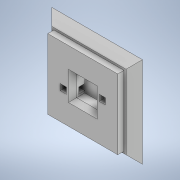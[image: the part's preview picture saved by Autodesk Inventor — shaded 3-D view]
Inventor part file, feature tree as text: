
AUTODESK INVENTOR PART (.ipt)
format: ipt  version: 2021 (Build 250183000, 183)  size: 201,216 bytes
history: native  units: in
note: dims shown in document units (in); Inventor stores cm internally (conversion verified against a paired STEP export)
features: extrude x6, sketch x6, chamfer x5, projected_geometry x3
ambient origin geometry x8: Origin, YZ Plane, XZ Plane, XY Plane, X Axis, Y Axis, Z Axis, Center Point
bodies: Solid1 (feature_tree)
feature tree (20):
  extrude  "Extrusion1"  Depth=0.1575in
  chamfer  "Chamfer1"  Distance=0.1575in
  extrude  "Extrusion2"  Depth=0.1181in TaperAngle=0.0deg
  extrude  "Extrusion3"  Depth=0.0394in
  chamfer  "Chamfer2"  Distance=0.1181in
  extrude  "Extrusion4"  Depth=0.0394in
  extrude  "Extrusion5"  Depth=0.0394in
  chamfer  "Chamfer3"  Distance=0.1181in
  chamfer  "Chamfer4"  Distance=0.1181in
  extrude  "Extrusion6"  Depth=0.0394in
  chamfer  "Chamfer5"  Distance=0.0394in
  sketch  "Sketch1"  dims[d0=1.7323in d1=1.7323in d2=0.1575in d3=0.0in]
  sketch  "Sketch2"  dims[d4=0.1575in d5=0.0787in d6=45.0deg d8=0.1181in d9=0.0in]
  projected_geometry  "Projected Loop1"
  sketch  "Sketch3"  dims[d10=0.0394in d11=1.378in]
  projected_geometry  "Projected Loop2"
  sketch  "Sketch6"  dims[d12=1.3386in]
  sketch  "Sketch7"  dims[d13=1.3386in d14=0.1181in d15=0.0in]
  projected_geometry  "Projected Loop5"
  sketch  "Sketch8"  dims[d16=0.0787in d17=0.0787in d18=45.0deg d38=0.0394in d39=0.0394in d40=0.1181in d41=0.1181in d42=0.0394in d43=0.0394in d44=0.1181in d45=0.1181in d46=0.1969in d47=0.0in d48=0.0787in d49=0.2362in d50=0.0in d51=0.0394in d52=0.0787in d53=45.0deg d54=0.0394in d55=0.0787in d56=45.0deg d57=0.0787in d58=0.2362in d59=0.0in d60=0.0394in d61=0.0787in d62=45.0deg]
